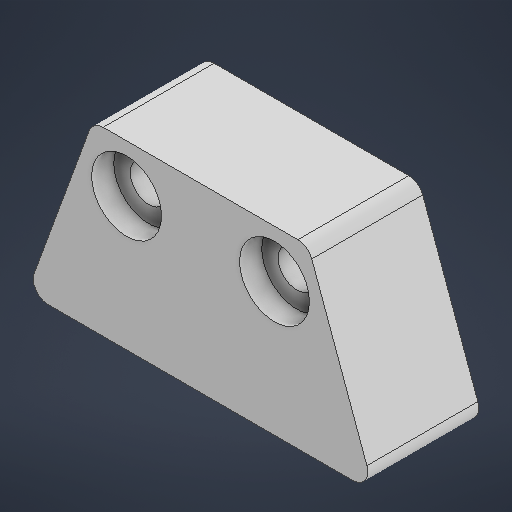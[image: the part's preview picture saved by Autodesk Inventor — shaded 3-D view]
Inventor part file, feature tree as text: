
AUTODESK INVENTOR PART (.ipt)
format: ipt  version: 2025.3 (Build 293356030, 356C)  size: 200,704 bytes
history: native  units: mm
features: extrude x2, sketch x1
ambient origin geometry x8: Origin, YZ Plane, XZ Plane, XY Plane, X Axis, Y Axis, Z Axis, Center Point
bodies: Solid1 (feature_tree)
feature tree (3):
  sketch  "Sketch1"  dims[d1=18.9mm d3=3.5mm d4=36.0mm d7=10.0mm d8=40.0mm d10=4.0mm d11=13.0mm d12=12.217305mm d13=30.0mm d14=0.0mm d15=18.0mm d16=0.0mm]
  extrude  "Extrusion1"  Depth=18.0mm
  extrude  "Extrusion2"  Depth=18.0mm
